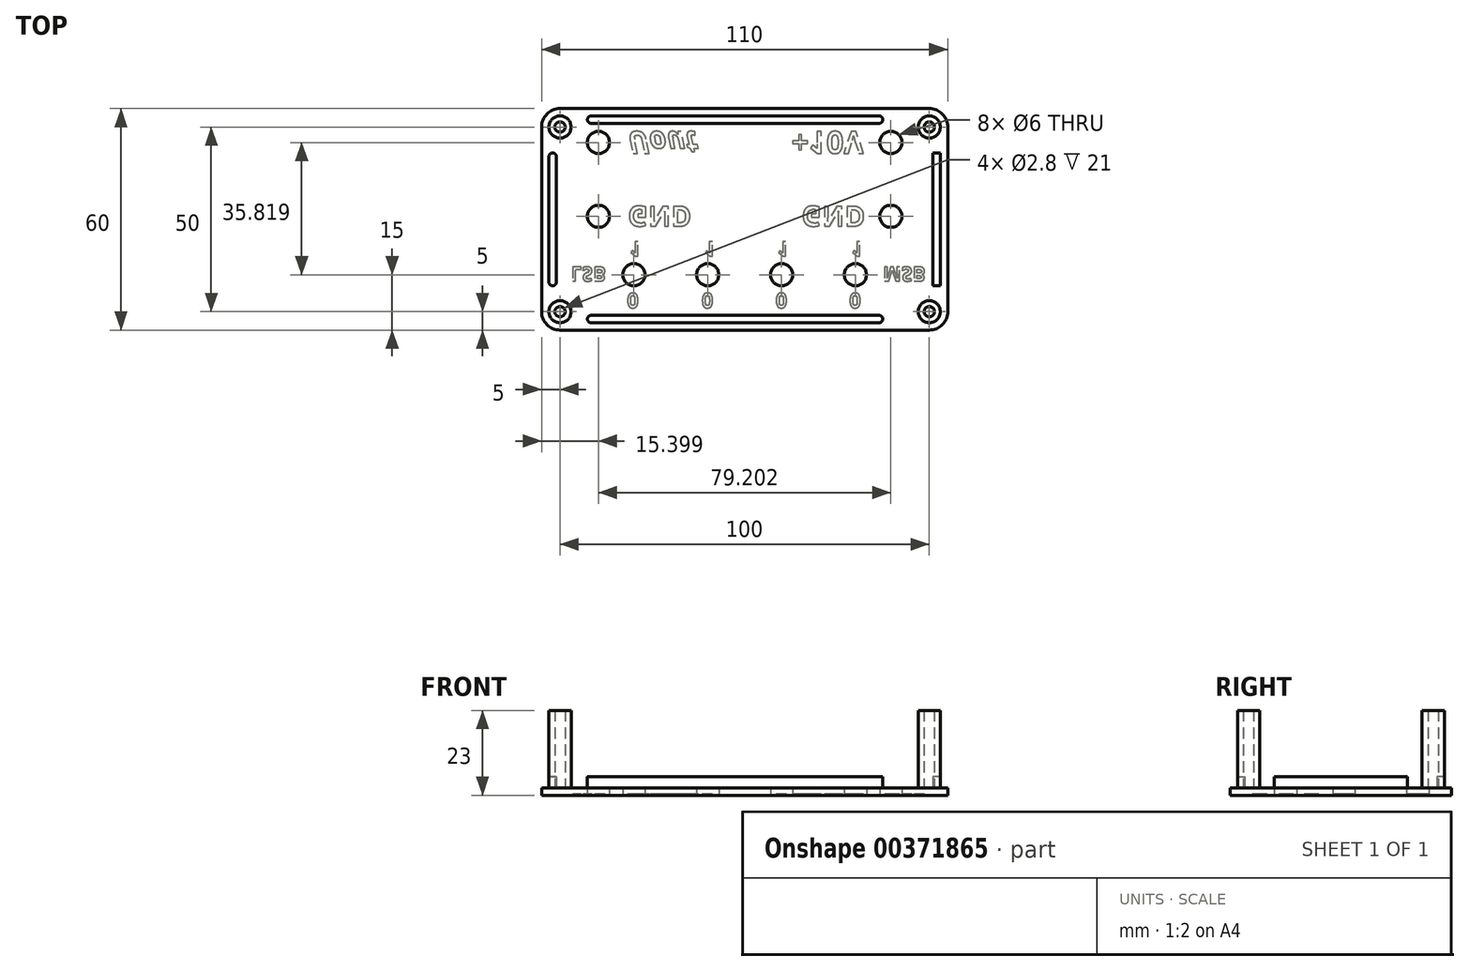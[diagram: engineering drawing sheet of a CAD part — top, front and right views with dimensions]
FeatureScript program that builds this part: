
annotation { "Feature Type Name" : "Feature", "Feature Type Description" : "" }
export const myFeature = defineFeature(function(context is Context, id is Id, definition is map)
    precondition{}
    {
        {
            var Q0;
            Q0=qCreatedBy(makeId("Top.planeOp"),FACE);
            var sketch = newSketch(context, id + "F0", { "sketchPlane" : qUnion([Q0])});
            skLineSegment(sketch, "E0.bottom", {"start": v(37.2, -21.36) * mm, "end": v(-37.2, -21.36) * mm, "construction": true});
            skLineSegment(sketch, "E0.top", {"start": v(37.2, 21.36) * mm, "end": v(-37.2, 21.36) * mm, "construction": true});
            skLineSegment(sketch, "E0.left", {"start": v(37.2, -21.36) * mm, "end": v(37.2, 21.36) * mm, "construction": true});
            skLineSegment(sketch, "E0.right", {"start": v(-37.2, -21.36) * mm, "end": v(-37.2, 21.36) * mm, "construction": true});
            skPoint(sketch, "E0.middle", {"position": v(0, 0) * mm});
            skCircle(sketch, "E1", {"center": v(-34.16, 18.25) * mm, "radius": 1.6 * mm, "construction": true});
            skCircle(sketch, "E2.MirrorC", {"center": v(34.16, 18.25) * mm, "radius": 1.6 * mm, "construction": true});
            skCircle(sketch, "E3.MirrorC", {"center": v(34.16, -18.25) * mm, "radius": 1.6 * mm, "construction": true});
            skCircle(sketch, "E4.MirrorC", {"center": v(-34.16, -18.25) * mm, "radius": 1.6 * mm, "construction": true});
            skLineSegment(sketch, "E5.bottom", {"start": v(-30.2, 21.36) * mm, "end": v(30.06, 21.36) * mm, "construction": true});
            skLineSegment(sketch, "E5.top", {"start": v(-30.2, -21.36) * mm, "end": v(30.06, -21.36) * mm, "construction": true});
            skLineSegment(sketch, "E5.left", {"start": v(-30.2, 21.36) * mm, "end": v(-30.2, -21.36) * mm, "construction": true});
            skLineSegment(sketch, "E5.right", {"start": v(30.06, 21.36) * mm, "end": v(30.06, -21.36) * mm, "construction": true});
            skLineSegment(sketch, "E6.bottom", {"start": v(-21.9, 18.36) * mm, "end": v(27.06, 18.36) * mm, "construction": true});
            skLineSegment(sketch, "E6.top", {"start": v(-21.9, -18.36) * mm, "end": v(27.06, -18.36) * mm, "construction": true});
            skLineSegment(sketch, "E6.left", {"start": v(-21.9, 18.36) * mm, "end": v(-21.9, -18.36) * mm, "construction": true});
            skLineSegment(sketch, "E6.right", {"start": v(27.06, 18.36) * mm, "end": v(27.06, -18.36) * mm, "construction": true});
            skLineSegment(sketch, "E7", {"start": v(-69.3, 0) * mm, "end": v(67.55, 0) * mm, "construction": true});
            skLineSegment(sketch, "E8", {"start": v(2.58, -33.09) * mm, "end": v(2.58, 37.46) * mm, "construction": true});
            skLineSegment(sketch, "E9.bottom", {"start": v(-21.9, 18.36) * mm, "end": v(27.06, 18.36) * mm});
            skLineSegment(sketch, "E9.top", {"start": v(-21.9, -18.36) * mm, "end": v(27.06, -18.36) * mm});
            skLineSegment(sketch, "E9.left", {"start": v(-21.9, 18.36) * mm, "end": v(-21.9, -18.36) * mm});
            skLineSegment(sketch, "E9.right", {"start": v(27.06, 18.36) * mm, "end": v(27.06, -18.36) * mm});
            skLineSegment(sketch, "E10.bottom", {"start": v(57.58, -30) * mm, "end": v(-52.42, -30) * mm});
            skLineSegment(sketch, "E10.top", {"start": v(57.58, 30) * mm, "end": v(-52.42, 30) * mm});
            skLineSegment(sketch, "E10.left", {"start": v(57.58, -30) * mm, "end": v(57.58, 30) * mm});
            skLineSegment(sketch, "E10.right", {"start": v(-52.42, -30) * mm, "end": v(-52.42, 30) * mm});
            skPoint(sketch, "E10.middle", {"position": v(2.58, 0) * mm});
            skSolve(sketch);
        }
        {
            var Q0;
            Q0=makeQuery(id+"F0.imprint","IMPRINT",FACE,{"disambiguationData":[TD([[makeQuery(id+"F0.imprint","IMPRINT",EDGE,{"derivedFrom":sQuery(id+"F0.wireOp",EDGE,"E9.bottom")}),1.0]])]});
            var Q1;
            Q1=makeQuery(id+"F0.imprint","IMPRINT",FACE,{"disambiguationData":[TD([[makeQuery(id+"F0.imprint","IMPRINT",EDGE,{"derivedFrom":sQuery(id+"F0.wireOp",EDGE,"E9.bottom")}),-1.0]])]});
            extrude(context, id + "F1", {"entities" : qUnion([Q0, Q1]), "offsetDistance" : 25 * mm, "depth" : 2 * mm});
        }
        {
            var Q0;
            Q0=makeQuery(id+"F1.opExtrude","SWEPT_EDGE",EDGE,{"disambiguationData":[OSD([sQuery(id+"F0.wireOp",EDGE,"E10.top"),sQuery(id+"F0.wireOp",EDGE,"E10.left")])]});
            var Q1;
            Q1=makeQuery(id+"F1.opExtrude","SWEPT_EDGE",EDGE,{"disambiguationData":[OSD([sQuery(id+"F0.wireOp",EDGE,"E10.top"),sQuery(id+"F0.wireOp",EDGE,"E10.right")])]});
            var Q2;
            Q2=makeQuery(id+"F1.opExtrude","SWEPT_EDGE",EDGE,{"disambiguationData":[OSD([sQuery(id+"F0.wireOp",EDGE,"E10.bottom"),sQuery(id+"F0.wireOp",EDGE,"E10.right")])]});
            var Q3;
            Q3=makeQuery(id+"F1.opExtrude","SWEPT_EDGE",EDGE,{"disambiguationData":[OSD([sQuery(id+"F0.wireOp",EDGE,"E10.bottom"),sQuery(id+"F0.wireOp",EDGE,"E10.left")])]});
            fillet(context, id + "F2", {"entities" : qUnion([Q0, Q1, Q2, Q3]), "radius" : 5 * mm, "tangentPropagation" : true, "allowEdgeOverflow" : false});
        }
        {
            var Q0;
            {var subQ0=sQuery(id+"F0.wireOp",EDGE,"zpZsg9xE-iQUr-hMDx-4yTp-kwfv9a1k3Hto");var subQ1=sQuery(id+"F0.wireOp",EDGE,"E10.right");var subQ2=sQuery(id+"F0.wireOp",EDGE,"E10.left");var subQ3=sQuery(id+"F0.wireOp",EDGE,"E10.top");var subQ4=sQuery(id+"F0.wireOp",EDGE,"E10.bottom");var subQ5=sQuery(id+"F0.wireOp",EDGE,"v62mlMx0-zebu-okq2-FoMi-auxJvthpUieG");var subQ6=sQuery(id+"F0.wireOp",EDGE,"E9.bottom");var subQ7=sQuery(id+"F0.wireOp",EDGE,"E9.right");var subQ8=sQuery(id+"F0.wireOp",EDGE,"E9.top");var subQ9=sQuery(id+"F0.wireOp",EDGE,"E9.left");var subQ10=sQuery(id+"F0.wireOp",EDGE,"qMjBRCcc-lWBf-kRpo-uLkv-zHoKJKTILuRE");var subQ11=sQuery(id+"F0.wireOp",EDGE,"fnRMTj3t-sgWX-KTiA-dPVG-LLRJFn4VET2m");Q0=makeQuery(id+"FPzb4hWC4ZVA2bK_5.boolean.opBoolean","SPLIT",FACE,{"disambiguationData":[TD([makeQuery(id+"F1.opExtrude","SWEPT_FACE",FACE,{"disambiguationData":[OSD([subQ6])]})])],"derivedFrom":makeQuery(id+"F1.opExtrude","CAP_FACE",FACE,{"disambiguationData":[OSD([subQ6,subQ8,subQ9,subQ7,subQ4,subQ3,subQ2,subQ1,subQ0,subQ5,subQ10,subQ11])],"isStart":false})});}
            var sketch = newSketch(context, id + "F3", { "sketchPlane" : qUnion([Q0])});
            skLineSegment(sketch, "E11.bottom", {"start": v(52.58, -25) * mm, "end": v(-47.42, -25) * mm, "construction": true});
            skLineSegment(sketch, "E11.top", {"start": v(52.58, 25) * mm, "end": v(-47.42, 25) * mm, "construction": true});
            skLineSegment(sketch, "E11.left", {"start": v(52.58, -25) * mm, "end": v(52.58, 25) * mm, "construction": true});
            skLineSegment(sketch, "E11.right", {"start": v(-47.42, -25) * mm, "end": v(-47.42, 25) * mm, "construction": true});
            skCircle(sketch, "E12", {"center": v(52.58, 25) * mm, "radius": 3 * mm});
            skCircle(sketch, "E13", {"center": v(52.58, -25) * mm, "radius": 3 * mm});
            skCircle(sketch, "E14", {"center": v(-47.42, -25) * mm, "radius": 3 * mm});
            skCircle(sketch, "E15", {"center": v(-47.42, 25) * mm, "radius": 3 * mm});
            skCircle(sketch, "E16", {"center": v(52.58, -25) * mm, "radius": 1.4 * mm});
            skCircle(sketch, "E17", {"center": v(-47.42, -25) * mm, "radius": 1.4 * mm});
            skCircle(sketch, "E18", {"center": v(52.58, 25) * mm, "radius": 1.4 * mm});
            skCircle(sketch, "E19", {"center": v(-47.42, 25) * mm, "radius": 1.4 * mm});
            skSolve(sketch);
        }
        {
            var Q0;
            Q0=qSketchRegion(id+"F3",true);
            extrude(context, id + "F4", {"entities" : qUnion([Q0]), "operationType" : NewBodyOperationType.ADD, "depth" : 21 * mm});
        }
        {
            var Q0;
            Q0=makeQuery(id+"F1.opExtrude","CAP_FACE",FACE,{"disambiguationData":[OSD([sQuery(id+"F0.wireOp",EDGE,"E10.bottom"),sQuery(id+"F0.wireOp",EDGE,"E10.top"),sQuery(id+"F0.wireOp",EDGE,"E10.left"),sQuery(id+"F0.wireOp",EDGE,"E10.right")])],"isStart":true});
            var sketch = newSketch(context, id + "F5", { "sketchPlane" : qUnion([Q0])});
            skLineSegment(sketch, "E20", {"start": v(2.58, -30) * mm, "end": v(2.58, 30) * mm, "construction": true});
            skLineSegment(sketch, "E21", {"start": v(57.58, 15) * mm, "end": v(-52.42, 15) * mm, "construction": true});
            skCircle(sketch, "E22", {"center": v(12.58, 15) * mm, "radius": 3 * mm});
            skCircle(sketch, "E23", {"center": v(32.58, 15) * mm, "radius": 3 * mm});
            skCircle(sketch, "E24.MirrorC", {"center": v(-7.42, 15) * mm, "radius": 3 * mm});
            skCircle(sketch, "E25.MirrorC", {"center": v(-27.42, 15) * mm, "radius": 3 * mm});
            skLineSegment(sketch, "E26", {"start": v(42.18, -30) * mm, "end": v(42.18, 30) * mm, "construction": true});
            skCircle(sketch, "E27", {"center": v(42.18, -20.82) * mm, "radius": 3 * mm});
            skCircle(sketch, "E28", {"center": v(42.18, -0.82) * mm, "radius": 3 * mm});
            skCircle(sketch, "E29.MirrorC", {"center": v(-37.02, -20.82) * mm, "radius": 3 * mm});
            skCircle(sketch, "E30.MirrorC", {"center": v(-37.02, -0.82) * mm, "radius": 3 * mm});
            skSolve(sketch);
        }
        {
            var Q0;
            Q0 = qSketchRegion(id + "F5", true);
            extrude(context, id + "F6", {"entities" : qUnion([Q0]), "operationType" : NewBodyOperationType.REMOVE, "endBound" : BoundingType.THROUGH_ALL, "oppositeDirection" : true, "depth" : 25 * mm, "offsetDistance" : 25 * mm});
        }
        {
            var Q0;
            Q0=makeQuery(id+"F1.opExtrude","CAP_FACE",FACE,{"disambiguationData":[OSD([sQuery(id+"F0.wireOp",EDGE,"E10.bottom"),sQuery(id+"F0.wireOp",EDGE,"E10.top"),sQuery(id+"F0.wireOp",EDGE,"E10.left"),sQuery(id+"F0.wireOp",EDGE,"E10.right")])],"isStart":true});
            var sketch = newSketch(context, id + "F7", { "sketchPlane" : qUnion([Q0])});
            skLineSegment(sketch, "E31.bottom", {"start": v(57.58, 20) * mm, "end": v(-51.43, 20) * mm, "construction": true});
            skLineSegment(sketch, "E31.top", {"start": v(57.58, 24) * mm, "end": v(-51.43, 24) * mm, "construction": true});
            skLineSegment(sketch, "E31.left", {"start": v(57.58, 20) * mm, "end": v(57.58, 24) * mm, "construction": true});
            skLineSegment(sketch, "E31.right", {"start": v(-51.43, 20) * mm, "end": v(-51.43, 24) * mm, "construction": true});
            skText(sketch, "E32", { "text": "0", "fontName": "OpenSans-Bold.ttf"});
            skText(sketch, "E33", { "text": "0", "fontName": "OpenSans-Bold.ttf"});
            skText(sketch, "E34", { "text": "0", "fontName": "OpenSans-Bold.ttf"});
            skText(sketch, "E35", { "text": "0", "fontName": "OpenSans-Bold.ttf"});
            skLineSegment(sketch, "E36", {"start": v(32.58, 15) * mm, "end": v(-27.42, 15) * mm, "construction": true});
            skLineSegment(sketch, "E37.MirrorCS", {"start": v(57.58, 10) * mm, "end": v(-51.43, 10) * mm, "construction": true});
            skLineSegment(sketch, "E38.MirrorCS", {"start": v(57.58, 6) * mm, "end": v(-51.43, 6) * mm, "construction": true});
            skText(sketch, "E39", { "text": "1", "fontName": "OpenSans-Bold.ttf"});
            skText(sketch, "E40", { "text": "1", "fontName": "OpenSans-Bold.ttf"});
            skText(sketch, "E41", { "text": "1", "fontName": "OpenSans-Bold.ttf"});
            skText(sketch, "E42", { "text": "1", "fontName": "OpenSans-Bold.ttf"});
            skLineSegment(sketch, "E43.bottom", {"start": v(-34.88, 12.92) * mm, "end": v(-44.5, 12.92) * mm, "construction": true});
            skLineSegment(sketch, "E43.top", {"start": v(-34.88, 16.76) * mm, "end": v(-44.5, 16.76) * mm, "construction": true});
            skLineSegment(sketch, "E43.left", {"start": v(-34.88, 12.92) * mm, "end": v(-34.88, 16.76) * mm, "construction": true});
            skLineSegment(sketch, "E43.right", {"start": v(-44.5, 12.92) * mm, "end": v(-44.5, 16.76) * mm, "construction": true});
            skLineSegment(sketch, "E44", {"start": v(2.58, -30) * mm, "end": v(2.58, 30) * mm, "construction": true});
            skLineSegment(sketch, "E45.MirrorCS", {"start": v(40.04, 12.92) * mm, "end": v(40.04, 16.76) * mm, "construction": true});
            skLineSegment(sketch, "E46.MirrorCS", {"start": v(40.04, 12.92) * mm, "end": v(49.65, 12.92) * mm, "construction": true});
            skLineSegment(sketch, "E47.MirrorCS", {"start": v(49.65, 12.92) * mm, "end": v(49.65, 16.76) * mm, "construction": true});
            skLineSegment(sketch, "E48.MirrorCS", {"start": v(40.04, 16.76) * mm, "end": v(49.65, 16.76) * mm, "construction": true});
            skText(sketch, "E49", { "text": "LSB", "fontName": "OpenSans-Bold.ttf"});
            skText(sketch, "E50", { "text": "MSB", "fontName": "OpenSans-Bold.ttf"});
            skLineSegment(sketch, "E51.bottom", {"start": v(41.8, -23.8) * mm, "end": v(-37.42, -23.8) * mm, "construction": true});
            skLineSegment(sketch, "E51.top", {"start": v(41.8, -17.85) * mm, "end": v(-37.42, -17.85) * mm, "construction": true});
            skLineSegment(sketch, "E51.left", {"start": v(41.8, -23.8) * mm, "end": v(41.8, -17.85) * mm, "construction": true});
            skLineSegment(sketch, "E51.right", {"start": v(-37.42, -23.8) * mm, "end": v(-37.42, -17.85) * mm, "construction": true});
            skLineSegment(sketch, "E52.bottom", {"start": v(43.42, -3.55) * mm, "end": v(-35.78, -3.55) * mm, "construction": true});
            skLineSegment(sketch, "E52.top", {"start": v(43.42, 1.91) * mm, "end": v(-35.78, 1.91) * mm, "construction": true});
            skLineSegment(sketch, "E52.left", {"start": v(43.42, -3.55) * mm, "end": v(43.42, 1.91) * mm, "construction": true});
            skLineSegment(sketch, "E52.right", {"start": v(-35.78, -3.55) * mm, "end": v(-35.78, 1.91) * mm, "construction": true});
            skText(sketch, "E53", { "text": "Uout", "fontName": "OpenSans-BoldItalic.ttf"});
            skText(sketch, "E54", { "text": "GND", "fontName": "OpenSans-Bold.ttf"});
            skText(sketch, "E55", { "text": "+10V", "fontName": "OpenSans-Bold.ttf"});
            skText(sketch, "E56", { "text": "GND", "fontName": "OpenSans-Bold.ttf"});
            const initialGuessF7  = {"E32": [0.0309, 0.02, 1, 0, 0.004], "E33": [0.01094, 0.02, 1, 0, 0.004], "E34": [-0.00908, 0.02, 1, 0, 0.004], "E35": [-0.0293, 0.02, 1, 0, 0.004], "E39": [0.03147, 0.006, 1, 0, 0.004], "E40": [0.0114, 0.006, 1, 0, 0.004], "E41": [-0.00843, 0.006, 1, 0, 0.004], "E42": [-0.0286, 0.006, 1, 0, 0.004], "E49": [-0.0445, 0.01292, 1, 0, 0.00384], "E50": [0.04004, 0.01292, 1, 0, 0.00384], "E53": [-0.02908, -0.0238, 1, 0, 0.00595], "E54": [-0.02908, -0.00355, 1, 0, 0.00546], "E55": [0.01525, -0.0238, 1, 0, 0.00595], "E56": [0.01798, -0.00355, 1, 0, 0.00546]};
            skSetInitialGuess(sketch, initialGuessF7);
            skSolve(sketch);
        }
        {
            var Q0;
            Q0 = qSketchRegion(id + "F7", true);
            extrude(context, id + "F8", {"entities" : qUnion([Q0]), "operationType" : NewBodyOperationType.REMOVE, "oppositeDirection" : true, "depth" : 0.4 * mm, "offsetDistance" : 25 * mm});
        }
        {
            var Q0;
            {var subQ0=sQuery(id+"F0.wireOp",EDGE,"E10.right");var subQ1=sQuery(id+"F0.wireOp",EDGE,"E10.top");var subQ2=sQuery(id+"F0.wireOp",EDGE,"E10.left");var subQ3=sQuery(id+"F0.wireOp",EDGE,"E10.bottom");Q0=makeQuery(id+"F4.boolean.opBoolean","SPLIT",FACE,{"disambiguationData":[TD([makeQuery(id+"F1.opExtrude","SWEPT_FACE",FACE,{"disambiguationData":[OSD([subQ3])]})])],"derivedFrom":makeQuery(id+"F1.opExtrude","CAP_FACE",FACE,{"disambiguationData":[OSD([subQ3,subQ1,subQ2,subQ0])],"isStart":false})});}
            var sketch = newSketch(context, id + "F9", { "sketchPlane" : qUnion([Q0])});
            skLineSegment(sketch, "E57.bottom", {"start": v(-50.42, 18) * mm, "end": v(-48.42, 18) * mm});
            skLineSegment(sketch, "E57.top", {"start": v(-50.42, -18) * mm, "end": v(-48.42, -18) * mm});
            skLineSegment(sketch, "E57.left", {"start": v(-50.42, 18) * mm, "end": v(-50.42, -18) * mm});
            skLineSegment(sketch, "E57.right", {"start": v(-48.42, 18) * mm, "end": v(-48.42, -18) * mm});
            skLineSegment(sketch, "E58", {"start": v(-52.42, 0) * mm, "end": v(57.58, 0) * mm, "construction": true});
            skLineSegment(sketch, "E59.bottom", {"start": v(-40, 28) * mm, "end": v(40, 28) * mm});
            skLineSegment(sketch, "E59.top", {"start": v(-40, 26) * mm, "end": v(40, 26) * mm});
            skLineSegment(sketch, "E59.left", {"start": v(-40, 28) * mm, "end": v(-40, 26) * mm});
            skLineSegment(sketch, "E59.right", {"start": v(40, 28) * mm, "end": v(40, 26) * mm});
            skLineSegment(sketch, "E60.MirrorCS", {"start": v(-40, -26) * mm, "end": v(40, -26) * mm});
            skLineSegment(sketch, "E61.MirrorCS", {"start": v(-40, -28) * mm, "end": v(40, -28) * mm});
            skLineSegment(sketch, "E62.MirrorCS", {"start": v(-40, -28) * mm, "end": v(-40, -26) * mm});
            skLineSegment(sketch, "E63.MirrorCS", {"start": v(40, -28) * mm, "end": v(40, -26) * mm});
            skLineSegment(sketch, "E64", {"start": v(2.58, 30) * mm, "end": v(2.58, -30) * mm, "construction": true});
            skLineSegment(sketch, "E65.MirrorCS", {"start": v(53.58, 18) * mm, "end": v(53.58, -18) * mm});
            skLineSegment(sketch, "E66.MirrorCS", {"start": v(55.58, 18) * mm, "end": v(55.58, -18) * mm});
            skLineSegment(sketch, "E67.MirrorCS", {"start": v(55.58, 18) * mm, "end": v(53.58, 18) * mm});
            skLineSegment(sketch, "E68.MirrorCS", {"start": v(55.58, -18) * mm, "end": v(53.58, -18) * mm});
            skSolve(sketch);
        }
        {
            var Q0;
            Q0 = qSketchRegion(id + "F9", true);
            extrude(context, id + "F10", {"entities" : qUnion([Q0]), "operationType" : NewBodyOperationType.ADD, "depth" : 3 * mm, "offsetDistance" : 25 * mm});
        }
        {
            var Q0;
            Q0=makeQuery(id+"F10.opExtrude","SWEPT_EDGE",EDGE,{"disambiguationData":[OSD([sQuery(id+"F9.wireOp",EDGE,"E61.MirrorCS"),sQuery(id+"F9.wireOp",EDGE,"E62.MirrorCS")])]});
            var Q1;
            Q1=makeQuery(id+"F10.opExtrude","SWEPT_EDGE",EDGE,{"disambiguationData":[OSD([sQuery(id+"F9.wireOp",EDGE,"E61.MirrorCS"),sQuery(id+"F9.wireOp",EDGE,"E63.MirrorCS")])]});
            var Q2;
            Q2=makeQuery(id+"F10.opExtrude","SWEPT_EDGE",EDGE,{"disambiguationData":[OSD([sQuery(id+"F9.wireOp",EDGE,"22c1dfd6-2819-4801-9885-116c486f79b20.MirrorCS"),sQuery(id+"F9.wireOp",EDGE,"dcc1d5e5-4989-4de3-bd9c-50c4c680c36f0.MirrorCS")])]});
            var Q3;
            Q3=makeQuery(id+"F10.opExtrude","SWEPT_EDGE",EDGE,{"disambiguationData":[OSD([sQuery(id+"F9.wireOp",EDGE,"ee48af64-cf3e-4936-8b29-0a129580c9e70.MirrorCS"),sQuery(id+"F9.wireOp",EDGE,"dcc1d5e5-4989-4de3-bd9c-50c4c680c36f0.MirrorCS")])]});
            var Q4;
            Q4=makeQuery(id+"F10.opExtrude","SWEPT_EDGE",EDGE,{"disambiguationData":[OSD([sQuery(id+"F9.wireOp",EDGE,"E59.top"),sQuery(id+"F9.wireOp",EDGE,"E59.right")])]});
            var Q5;
            Q5=makeQuery(id+"F10.opExtrude","SWEPT_EDGE",EDGE,{"disambiguationData":[OSD([sQuery(id+"F9.wireOp",EDGE,"E59.top"),sQuery(id+"F9.wireOp",EDGE,"E59.left")])]});
            var Q6;
            Q6=makeQuery(id+"F10.opExtrude","SWEPT_EDGE",EDGE,{"disambiguationData":[OSD([sQuery(id+"F9.wireOp",EDGE,"E57.top"),sQuery(id+"F9.wireOp",EDGE,"E57.right")])]});
            var Q7;
            Q7=makeQuery(id+"F10.opExtrude","SWEPT_EDGE",EDGE,{"disambiguationData":[OSD([sQuery(id+"F9.wireOp",EDGE,"E57.top"),sQuery(id+"F9.wireOp",EDGE,"E57.left")])]});
            var Q8;
            Q8=makeQuery(id+"F10.opExtrude","SWEPT_EDGE",EDGE,{"disambiguationData":[OSD([sQuery(id+"F9.wireOp",EDGE,"E59.bottom"),sQuery(id+"F9.wireOp",EDGE,"E59.right")])]});
            var Q9;
            Q9=makeQuery(id+"F10.opExtrude","SWEPT_EDGE",EDGE,{"disambiguationData":[OSD([sQuery(id+"F9.wireOp",EDGE,"E59.bottom"),sQuery(id+"F9.wireOp",EDGE,"E59.left")])]});
            var Q10;
            Q10=makeQuery(id+"F10.opExtrude","SWEPT_EDGE",EDGE,{"disambiguationData":[OSD([sQuery(id+"F9.wireOp",EDGE,"E60.MirrorCS"),sQuery(id+"F9.wireOp",EDGE,"E62.MirrorCS")])]});
            var Q11;
            Q11=makeQuery(id+"F10.opExtrude","SWEPT_EDGE",EDGE,{"disambiguationData":[OSD([sQuery(id+"F9.wireOp",EDGE,"E60.MirrorCS"),sQuery(id+"F9.wireOp",EDGE,"E63.MirrorCS")])]});
            var Q12;
            Q12=makeQuery(id+"F10.opExtrude","SWEPT_EDGE",EDGE,{"disambiguationData":[OSD([sQuery(id+"F9.wireOp",EDGE,"22c1dfd6-2819-4801-9885-116c486f79b20.MirrorCS"),sQuery(id+"F9.wireOp",EDGE,"9405c1cc-a6e0-4711-9b2e-0c0aa00461080.MirrorCS")])]});
            var Q13;
            Q13=makeQuery(id+"F10.opExtrude","SWEPT_EDGE",EDGE,{"disambiguationData":[OSD([sQuery(id+"F9.wireOp",EDGE,"ee48af64-cf3e-4936-8b29-0a129580c9e70.MirrorCS"),sQuery(id+"F9.wireOp",EDGE,"9405c1cc-a6e0-4711-9b2e-0c0aa00461080.MirrorCS")])]});
            var Q14;
            Q14=makeQuery(id+"F10.opExtrude","SWEPT_EDGE",EDGE,{"disambiguationData":[OSD([sQuery(id+"F9.wireOp",EDGE,"E57.bottom"),sQuery(id+"F9.wireOp",EDGE,"E57.right")])]});
            var Q15;
            Q15=makeQuery(id+"F10.opExtrude","SWEPT_EDGE",EDGE,{"disambiguationData":[OSD([sQuery(id+"F9.wireOp",EDGE,"E57.bottom"),sQuery(id+"F9.wireOp",EDGE,"E57.left")])]});
            fillet(context, id + "F11", {"entities" : qUnion([Q0, Q1, Q2, Q3, Q4, Q5, Q6, Q7, Q8, Q9, Q10, Q11, Q12, Q13, Q14, Q15]), "tangentPropagation" : true, "radius" : 1 * mm, "defaultsChanged" : false, "vertexSettings" : [], "allowEdgeOverflow" : false});
        }
    });
